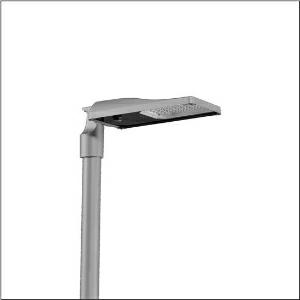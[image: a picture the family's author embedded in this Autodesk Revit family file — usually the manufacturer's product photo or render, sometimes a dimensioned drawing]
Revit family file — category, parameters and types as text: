
# Revit family: streetlight_sl_31_mini___st1_0a_5xh2d31r08ga_f9bd
name_source: partatom
category: Lighting Fixtures
units: mm (PartAtom-declared; Revit-internal decimal feet)

## family parameters
Cut with Voids When Loaded = No
Host = Face
Light Source = No
Part Type = Normal
Room Calculation Point = No
Round Connector Dimension = Use Diameter
Shared = No

## types (1)
- --- (1 x LED, 5880 lm, 39.3 W, 3000K)
    Apparent Load = 39 VA
    CIE Flux Codes = 37 72 97 100 100
    Color Rendering = 70
    Color Temperature = 3000K
    Default Elevation = 1800 mm
    Description = Streetlight SL 31 mini D4i, Desk-Remote mast luminaire for post-top, side-entry; light control with lens of PMMA; light distribution: ST1.0a, direct asymmetric distribution, for standard-compliant lighting for roads and squares; LED: luminous flux: 5.880lm, light colour: 730, colour temperature: 3000K; luminous efficacy: 149,6lm/W; control: pre-setting: logarithmic dimming characteristic, flexible luminous flux parameterisation, time-dependent luminous flux control, constant luminous flux control, power reduction, intelligent temperature release in ECG and LED module, overheat protection; luminaire housing, of diecast aluminium, SITECO metallic grey (DB 702S), corrosivity category C5 high according to DIN EN ISO 12944; cover of toughened safety glass, transparent, mast flange of diecast aluminium, SITECO metallic grey (DB 702S), spigot size: 76/60mm, mast flange included unmounted; with cable H07RN-F 2x 1.5mm², cable length: 6,5m, connection cable pre-assembled; mains connection: 220..240V, AC, 50/60Hz; power consumption (at start of service life): 39,3W / (at end of service life): 40,7W / (with reduced operation 50%): 18,1W; protection rating (complete): IP66; insulation class (complete): insulation class II (safety insulation); impact resistance: IK09; certification: CE, ENEC, ENEC+, VDE, UKCA, ZD4i; permissible operating ambient temperature for outdoor applications: -40..+50°C; packaging unit: 1 piece

Light Distribution: ST1.0a
    Height = 76 mm
    Lamp = 1 x LED
    Lamp Light Flux = 5880 lm
    Lamp Power = 39.3 W
    Lamp count = 1
    Length = 547 mm
    Luminous efficacy = 150 lm/W
    Manufacturer = Siteco
    ModVariant = No
    Model = 5XH2D31R08GA
    Number of Poles = 1
    OnlyDefault = Yes
    Power Factor = 1
    Product Name = Streetlight SL 31 mini | ST1.0a
    Product group = mast luminaire | pylon top
    ProductGroupID = 6100
    Protection Class = Protection class II
    Protection Degree = IP 66
    RLX_Detail_Level = 1
    RLX_Emergency_Light_Flux = 0 lm
    RLX_Emergency_Type = 0
    RLX_Emergency_Type_DB = No
    RlxData = <blob elided: 39729 chars, md5=b8f51078>
    Socket = socket
    Standby Power = 0 W
    System Light Flux = 5880 lm
    System Power = 39 W
    Type Comments = factory setting: luminous flux: 100 % | dim-lin: 254 | 798 mA
    Type Image = l_1300328.jpg
    URL = http://relux.com
    VarID = @adj_061573
    Voltage = 0 V
    Weight = 0.00 kg
    Width = 265 mm

## geometry (parser evidence)
native form markers: Blend x4, Sweep x9
no freeform markers — native parametric forms only
